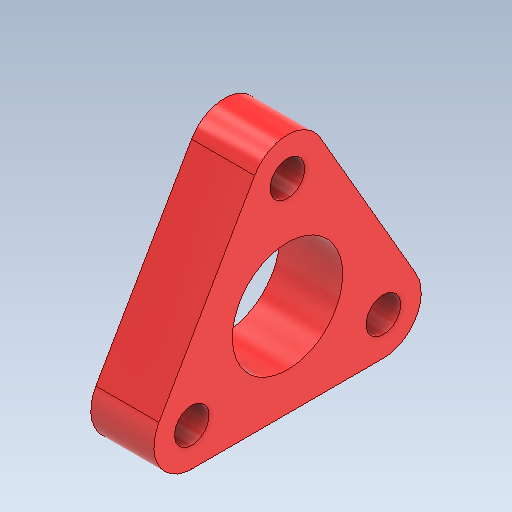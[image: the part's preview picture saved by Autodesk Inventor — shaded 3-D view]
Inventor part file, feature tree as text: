
AUTODESK INVENTOR PART (.ipt)
format: ipt  version: 2021 (Build 250183000, 183)  size: 142,848 bytes
history: native  units: in
note: dims shown in document units (in); Inventor stores cm internally (conversion verified against a paired STEP export)
features: sketch x2, extrude x1
ambient origin geometry x8: Origin, YZ Plane, XZ Plane, XY Plane, X Axis, Y Axis, Z Axis, Center Point
bodies: Solid1 (feature_tree)
feature tree (3):
  sketch  "Sketch1"  dims[d0=1.378in d1=2.7559in]
  extrude  "Extrusion1"  Depth=2.7559in
  sketch  "Sketch2"  dims[d2=0.4331in d3=1.1811in d5=360.0deg d7=0.9449in d8=0.9449in d9=0.9449in d10=0.7874in d11=0.0in]
